# Revit family: Tap-Sink Set-Caroma G Series Concealed 80 Lever (160 Outlet)-Wall_Temp_65347b36-99b5-4af6-a89e-ec3a5421b6c3
name_source: partatom
category: Plumbing Fixtures
revit_build: Autodesk Revit 2015 (Build: 20160512_1515(x64)
units: mm (PartAtom-declared; Revit-internal decimal feet)

## types (1)
- Chrome
    Assembly Code = D2020
    CW Connection = Yes
    CWFU = 0
    ColdWaterConnectorDiameter = 20 mm  [stored 0.0656168 ft]
    Cost = 0 $
    Default Elevation = 1000 mm  [stored 3.28084 ft]
    Description = WELS 4 star rated, 7.5L/min
    HW Connection = Yes
    HWFU = 0
    HotWaterConnectorDiameter = 20 mm  [stored 0.0656168 ft]
    Manufacturer = GWA Bathrooms&Kitchens
    Material_ANZRS = Metal-Chrome-Caroma
    Model = G92880C4A
    ModifiedIssue_ANZRS = 20170424.54 $
    Type Comments = Caroma G Series Plus Concealed Wall Sink Set 160 Outlet 80 Hdl
    URL = http://specify.caroma.com.au
    Vent Connection = No
    Waste Connection = No

note: [stored X ft] marks values corroborated as IEEE doubles in the binary element streams (Revit-internal decimal feet)

## geometry (parser evidence)
native form markers: Sweep x1
no freeform markers — native parametric forms only
